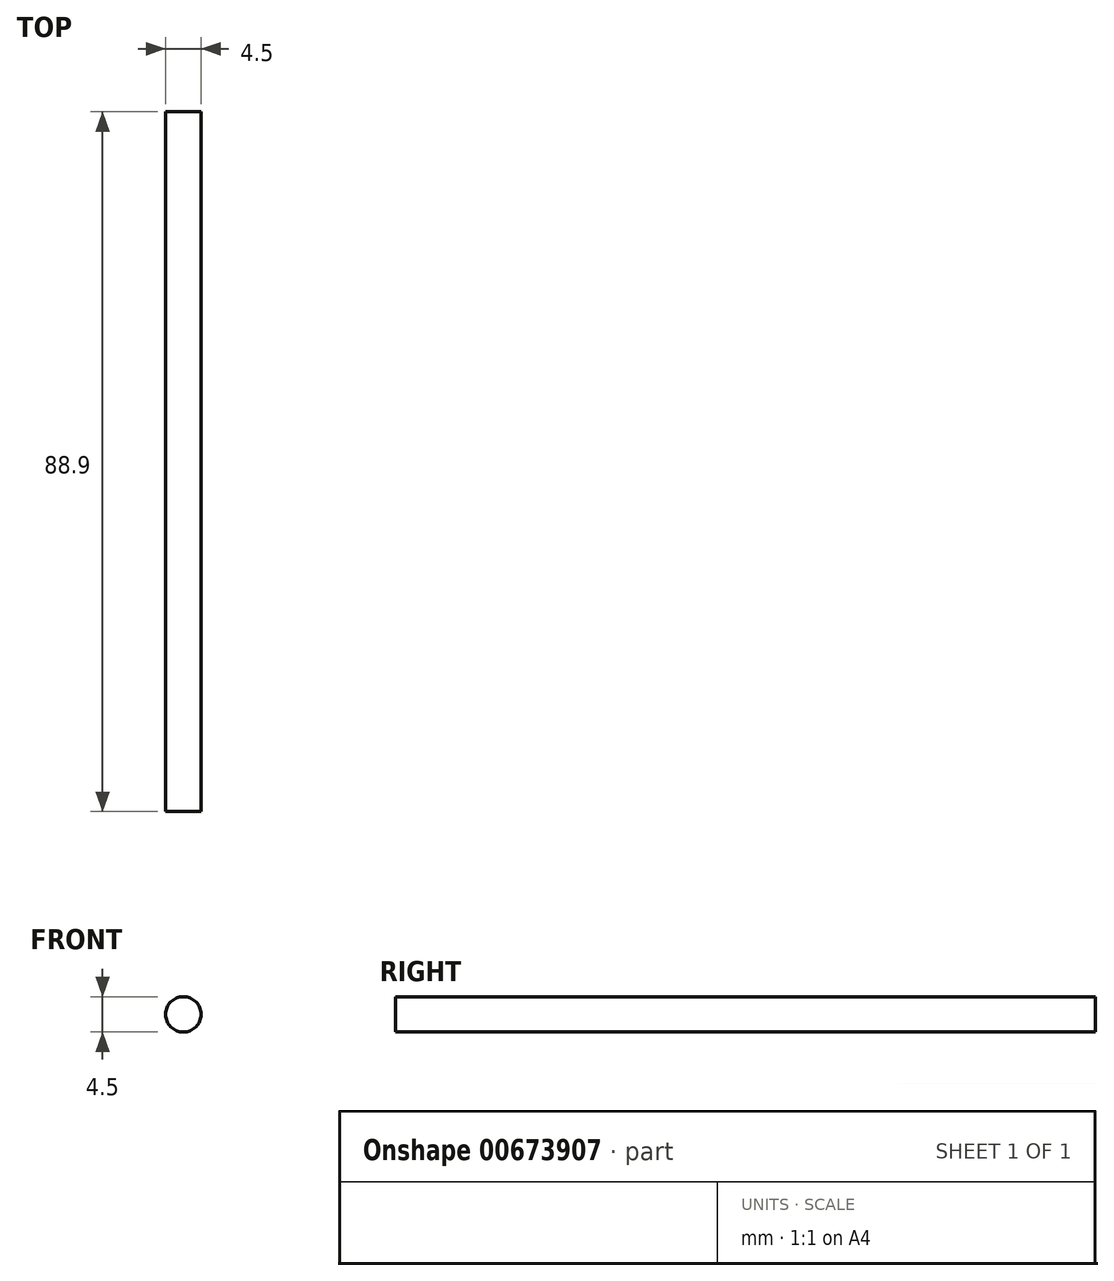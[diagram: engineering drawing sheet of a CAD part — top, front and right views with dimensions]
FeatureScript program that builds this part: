
annotation { "Feature Type Name" : "Feature", "Feature Type Description" : "" }
export const myFeature = defineFeature(function(context is Context, id is Id, definition is map)
    precondition{}
    {
        {
            var Q0;
            Q0=qCreatedBy(makeId("Front.planeOp"),FACE);
            var sketch = newSketch(context, id + "F0", { "sketchPlane" : qUnion([Q0])});
            skCircle(sketch, "E0", {"center": v(0, 0) * mm, "radius": 2.25 * mm});
            skSolve(sketch);
        }
        {
            var Q0;
            Q0 = qSketchRegion(id + "F0", true);
            extrude(context, id + "F1", {"entities" : qUnion([Q0]), "depth" : 88.9 * mm, "offsetDistance" : 25.4 * mm});
        }
    });
